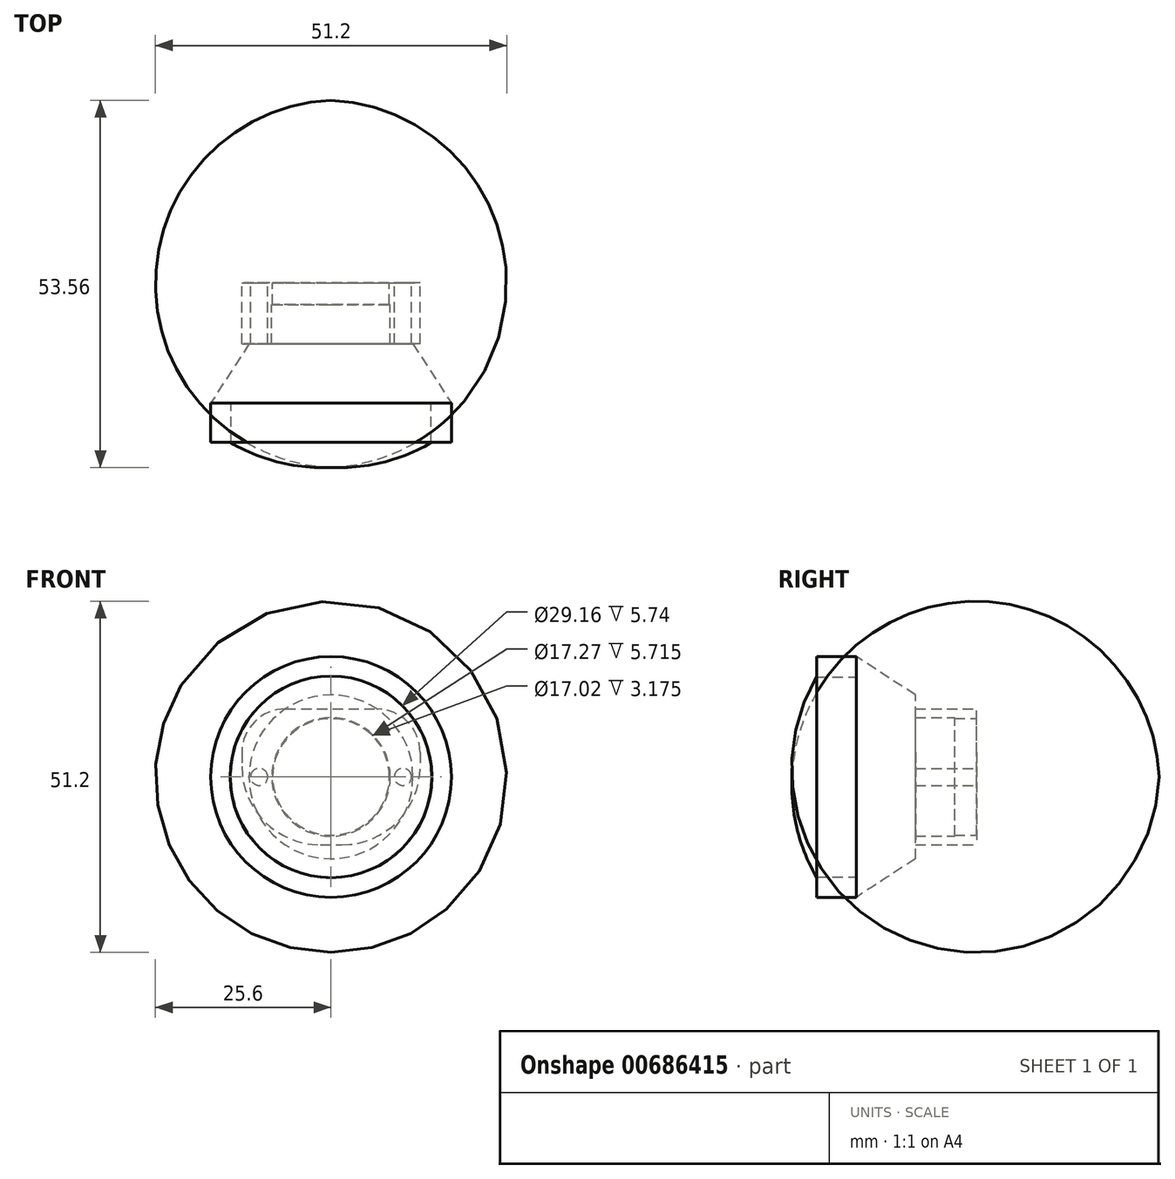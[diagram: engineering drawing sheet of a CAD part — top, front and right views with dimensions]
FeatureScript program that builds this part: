
annotation { "Feature Type Name" : "Feature", "Feature Type Description" : "" }
export const myFeature = defineFeature(function(context is Context, id is Id, definition is map)
    precondition{}
    {
        {
            var Q0;
            Q0=qCreatedBy(makeId("Front.planeOp"),FACE);
            var sketch = newSketch(context, id + "F0", { "sketchPlane" : qUnion([Q0])});
            skPoint(sketch, "E0.middle", {"position": v(0, 0) * mm});
            skCircle(sketch, "E1", {"center": v(0, 0) * mm, "radius": 8.5 * mm});
            skCircle(sketch, "E2", {"center": v(-10.48, 0) * mm, "radius": 1.24 * mm});
            skCircle(sketch, "E3", {"center": v(10.48, 0) * mm, "radius": 1.24 * mm});
            skLineSegment(sketch, "E4.bottom", {"start": v(-6.64, 9.9) * mm, "end": v(6.64, 9.9) * mm});
            skLineSegment(sketch, "E4.top", {"start": v(-1.56, -9.9) * mm, "end": v(1.56, -9.9) * mm});
            skLineSegment(sketch, "E4.left", {"start": v(-13, 3.56) * mm, "end": v(-13, 1.52) * mm});
            skLineSegment(sketch, "E4.right", {"start": v(13, 3.56) * mm, "end": v(13, 1.52) * mm});
            skPoint(sketch, "E5.visualSharp", {"position": v(-13, 9.9) * mm});
            skArc(sketch, "E5.filletArc", {"start": v(-6.64, 9.9) * mm, "mid": v(-11.13, 8.05) * mm, "end": v(-13, 3.56) * mm});
            skPoint(sketch, "E6.visualSharp", {"position": v(13, 9.9) * mm});
            skArc(sketch, "E6.filletArc", {"start": v(13, 3.56) * mm, "mid": v(11.13, 8.05) * mm, "end": v(6.64, 9.9) * mm});
            skPoint(sketch, "E7.visualSharp", {"position": v(13, -9.9) * mm});
            skArc(sketch, "E7.filletArc", {"start": v(1.56, -9.9) * mm, "mid": v(9.64, -6.56) * mm, "end": v(13, 1.52) * mm});
            skPoint(sketch, "E8.visualSharp", {"position": v(-13, -9.9) * mm});
            skArc(sketch, "E8.filletArc", {"start": v(-13, 1.52) * mm, "mid": v(-9.64, -6.56) * mm, "end": v(-1.56, -9.9) * mm});
            skCircle(sketch, "E9", {"center": v(0, 0) * mm, "radius": 8.64 * mm});
            skSolve(sketch);
        }
        {
            var Q0;
            Q0=makeQuery(id+"F0.imprint","IMPRINT",FACE,{"disambiguationData":[TD([[makeQuery(id+"F0.imprint","IMPRINT",EDGE,{"derivedFrom":sQuery(id+"F0.wireOp",EDGE,"E2")}),-1.0]])]});
            extrude(context, id + "F1", {"entities" : qUnion([Q0]), "depth" : 8.9 * mm});
        }
        {
            var Q0;
            Q0=makeQuery(id+"F0.imprint","IMPRINT",FACE,{"disambiguationData":[TD([[makeQuery(id+"F0.imprint","IMPRINT",EDGE,{"derivedFrom":sQuery(id+"F0.wireOp",EDGE,"E1")}),-1.0]])]});
            extrude(context, id + "F2", {"entities" : qUnion([Q0]), "operationType" : NewBodyOperationType.ADD, "depth" : 3.17 * mm});
        }
        {
            var Q0;
            Q0=makeQuery(id+"F1.opExtrude","CAP_FACE",FACE,{"disambiguationData":[OSD([sQuery(id+"F0.wireOp",EDGE,"E2"),sQuery(id+"F0.wireOp",EDGE,"E3"),sQuery(id+"F0.wireOp",EDGE,"E4.bottom"),sQuery(id+"F0.wireOp",EDGE,"E4.top"),sQuery(id+"F0.wireOp",EDGE,"E4.left"),sQuery(id+"F0.wireOp",EDGE,"E4.right"),sQuery(id+"F0.wireOp",EDGE,"E5.filletArc"),sQuery(id+"F0.wireOp",EDGE,"E6.filletArc"),sQuery(id+"F0.wireOp",EDGE,"E7.filletArc"),sQuery(id+"F0.wireOp",EDGE,"E8.filletArc"),sQuery(id+"F0.wireOp",EDGE,"E9")])],"isStart":false});
            var sketch = newSketch(context, id + "F3", { "sketchPlane" : qUnion([Q0])});
            skCircle(sketch, "E10", {"center": v(0, 0) * mm, "radius": 11.94 * mm});
            skSolve(sketch);
        }
        {
            var Q0;
            Q0=qSketchRegion(id+"F3",true);
            var Q1;
            Q1=sQuery(id+"F3.wireOp",EDGE,"E10");
            extrude(context, id + "F4", {"entities" : qUnion([Q0]), "surfaceEntities" : qUnion([Q1]), "depth" : 8.64 * mm, "hasDraft" : true, "draftAngle" : 33 * degree});
        }
        {
            var Q0;
            Q0=makeQuery(id+"F4.opExtrude","CAP_FACE",FACE,{"disambiguationData":[OSD([sQuery(id+"F3.wireOp",EDGE,"E10")])],"isStart":false});
            var sketch = newSketch(context, id + "F5", { "sketchPlane" : qUnion([Q0])});
            skCircle(sketch, "E11", {"center": v(0, 0) * mm, "radius": 17.55 * mm});
            skCircle(sketch, "E12", {"center": v(0, 0) * mm, "radius": 14.58 * mm});
            skSolve(sketch);
        }
        {
            var Q0;
            Q0=qSketchRegion(id+"F5",true);
            extrude(context, id + "F6", {"entities" : qUnion([Q0]), "operationType" : NewBodyOperationType.ADD, "depth" : 5.74 * mm});
        }
        {
            var Q0;
            Q0=qCreatedBy(makeId("Right.planeOp"),FACE);
            var sketch = newSketch(context, id + "F7", { "sketchPlane" : qUnion([Q0])});
            skArc(sketch, "E13", {"start": v(-26.9, 0) * mm, "mid": v(-26.14, -7.61) * mm, "end": v(-23.27, -14.7) * mm});
            skLineSegment(sketch, "E14", {"start": v(-23.27, -14.7) * mm, "end": v(-23.27, 0) * mm});
            skLineSegment(sketch, "E15", {"start": v(-23.27, 0) * mm, "end": v(-26.9, 0) * mm});
            skSolve(sketch);
        }
        {
            var Q0;
            Q0=makeQuery(id+"F7.imprint","IMPRINT",FACE,{"disambiguationData":[TD([[makeQuery(id+"F7.imprint","IMPRINT",EDGE,{"derivedFrom":sQuery(id+"F7.wireOp",EDGE,"E13")}),1.0]])]});
            var Q1;
            Q1=sQuery(id+"F7.wireOp",EDGE,"E15");
            revolve(context, id + "F8", {"entities" : qUnion([Q0]), "axis" : qUnion([Q1]), "revolveType" : RevolveType.FULL});
        }
    });
